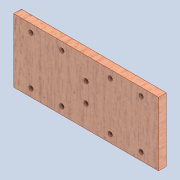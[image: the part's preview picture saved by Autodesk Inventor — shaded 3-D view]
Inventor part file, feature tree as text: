
AUTODESK INVENTOR PART (.ipt)
format: ipt  version: 2020 (Build 240168000, 168)  size: 239,104 bytes
history: native  units: mm
features: extrude x2, sketch x2
ambient origin geometry x8: Origin, YZ Plane, XZ Plane, XY Plane, X Axis, Y Axis, Z Axis, Center Point
bodies: Solid1 (feature_tree)
feature tree (4):
  extrude  "Extrusion1"  Depth=66.0mm
  extrude  "Extrusion4"  Depth=10.0mm
  sketch  "Sketch1"  dims[d0=150.0mm d1=66.0mm]
  sketch  "Sketch4"  dims[d2=8.0mm d3=0.0mm d19=4.5mm d20=18.0mm d21=8.0mm d22=8.0mm d23=32.0mm d24=18.0mm d26=32.0mm d27=0.0mm d28=0.0mm d29=10.0mm d30=10.0mm]
